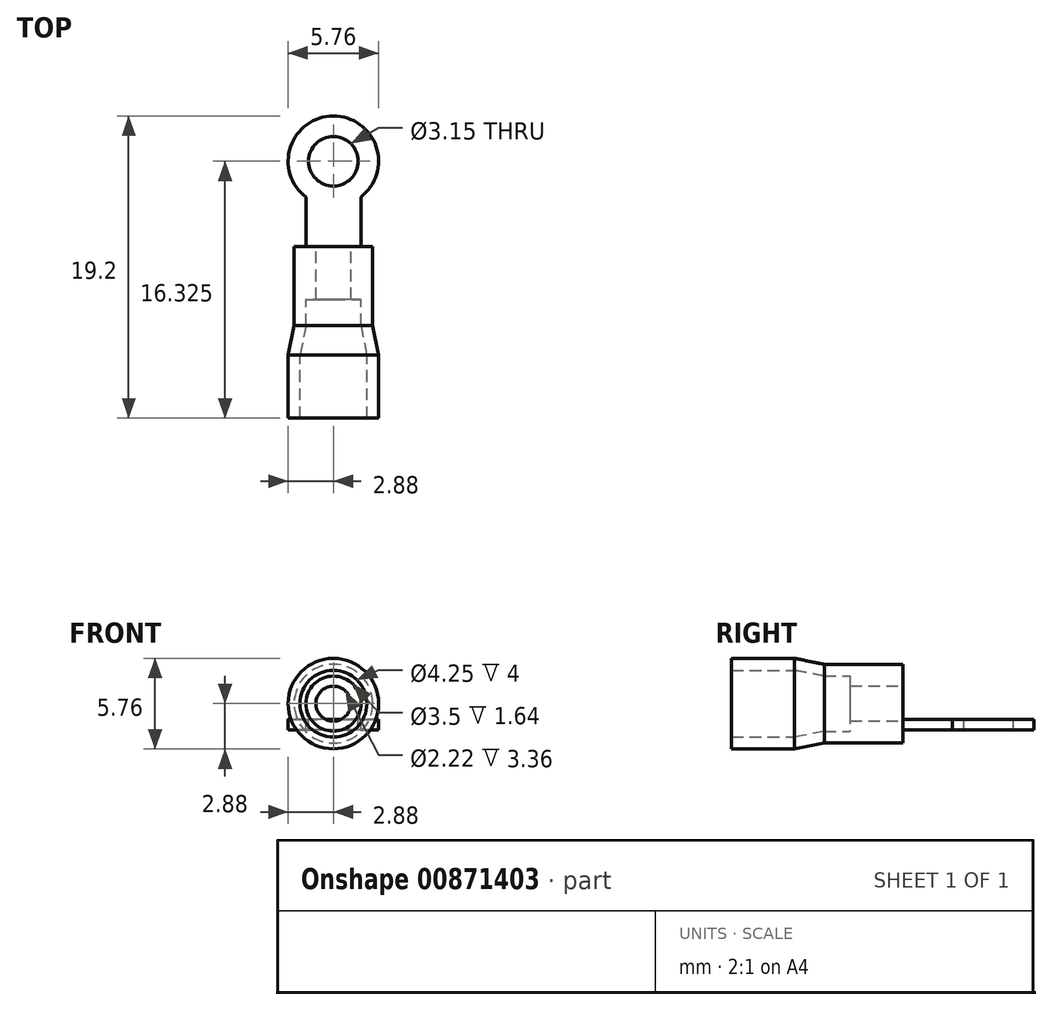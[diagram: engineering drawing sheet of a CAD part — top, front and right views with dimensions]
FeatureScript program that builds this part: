
annotation { "Feature Type Name" : "Feature", "Feature Type Description" : "" }
export const myFeature = defineFeature(function(context is Context, id is Id, definition is map)
    precondition{}
    {
        {
            var Q0;
            Q0=qCreatedBy(makeId("Top.planeOp"),FACE);
            var sketch = newSketch(context, id + "F0", { "sketchPlane" : qUnion([Q0])});
            skCircle(sketch, "E0", {"center": v(0, 5.42) * mm, "radius": 1.57 * mm});
            skCircle(sketch, "E1", {"center": v(0, 5.42) * mm, "radius": 2.87 * mm});
            skLineSegment(sketch, "E2", {"start": v(-1.75, 3.14) * mm, "end": v(-1.75, 0) * mm});
            skLineSegment(sketch, "E3", {"start": v(0, 5.42) * mm, "end": v(0, 0) * mm, "construction": true});
            skLineSegment(sketch, "E4", {"start": v(-1.75, 0) * mm, "end": v(0, 0) * mm});
            skLineSegment(sketch, "E5", {"start": v(-2.5, 0) * mm, "end": v(-2.5, -5) * mm});
            skLineSegment(sketch, "E6", {"start": v(-2.5, -5) * mm, "end": v(-2.87, -6.9) * mm});
            skLineSegment(sketch, "E7", {"start": v(-2.87, -6.9) * mm, "end": v(-2.87, -10.9) * mm});
            skLineSegment(sketch, "E8", {"start": v(-2.87, -10.9) * mm, "end": v(-2.12, -10.9) * mm});
            skLineSegment(sketch, "E9", {"start": v(-2.12, -10.9) * mm, "end": v(-2.12, -6.9) * mm});
            skLineSegment(sketch, "E10", {"start": v(-2.12, -6.9) * mm, "end": v(-1.75, -5) * mm});
            skLineSegment(sketch, "E11", {"start": v(-1.75, -5) * mm, "end": v(-1.75, 0) * mm});
            skLineSegment(sketch, "E12", {"start": v(-1.75, 0) * mm, "end": v(-2.5, 0) * mm});
            skLineSegment(sketch, "E13", {"start": v(-2.13, -6.9) * mm, "end": v(-2.87, -6.9) * mm, "construction": true});
            skLineSegment(sketch, "E14", {"start": v(-1.75, -5) * mm, "end": v(-2.5, -5) * mm, "construction": true});
            skLineSegment(sketch, "E15.MirrorCS", {"start": v(1.75, 3.14) * mm, "end": v(1.75, 0) * mm});
            skLineSegment(sketch, "E16.MirrorCS", {"start": v(1.75, 0) * mm, "end": v(0, 0) * mm});
            skLineSegment(sketch, "E17", {"start": v(-1.11, 0) * mm, "end": v(-1.11, -3.36) * mm});
            skLineSegment(sketch, "E18", {"start": v(-1.11, -3.36) * mm, "end": v(-1.75, -3.36) * mm});
            skSolve(sketch);
        }
        {
            var Q0;
            {var subQ3=sQuery(id+"F0.wireOp",EDGE,"E17");Q0=makeQuery(id+"F0.imprint","IMPRINT",FACE,{"disambiguationData":[TD([[makeQuery(id+"F0.imprint","IMPRINT",EDGE,{"derivedFrom":subQ3}),-1.0]])]});}
            var Q1;
            Q1=makeQuery(id+"F0.imprint","IMPRINT",FACE,{"disambiguationData":[TD([[makeQuery(id+"F0.imprint","IMPRINT",EDGE,{"derivedFrom":sQuery(id+"F0.wireOp",EDGE,"E5")}),1.0]])]});
            var Q2;
            Q2=sQuery(id+"F0.wireOp",EDGE,"E3");
            revolve(context, id + "F1", {"surfaceOperationType" : NewSurfaceOperationType.NEW, "entities" : qUnion([Q0, Q1]), "axis" : qUnion([Q2]), "revolveType" : RevolveType.FULL});
        }
        {
            var Q0;
            {var subQ3=sQuery(id+"F0.wireOp",EDGE,"E2");Q0=makeQuery(id+"F0.imprint","IMPRINT",FACE,{"disambiguationData":[TD([[makeQuery(id+"F0.imprint","IMPRINT",EDGE,{"derivedFrom":subQ3}),1.0]])]});}
            var Q1;
            Q1=makeQuery(id+"F0.imprint","IMPRINT",FACE,{"disambiguationData":[TD([[makeQuery(id+"F0.imprint","IMPRINT",EDGE,{"derivedFrom":sQuery(id+"F0.wireOp",EDGE,"E0")}),-1.0]])]});
            extrude(context, id + "F2", {"entities" : qUnion([Q0, Q1]), "operationType" : NewBodyOperationType.ADD, "oppositeDirection" : true, "depth" : 1.68 * mm, "offsetDistance" : 25 * mm, "hasSecondDirection" : true, "secondDirectionOppositeDirection" : true, "secondDirectionDepth" : 1 * mm});
        }
    });
